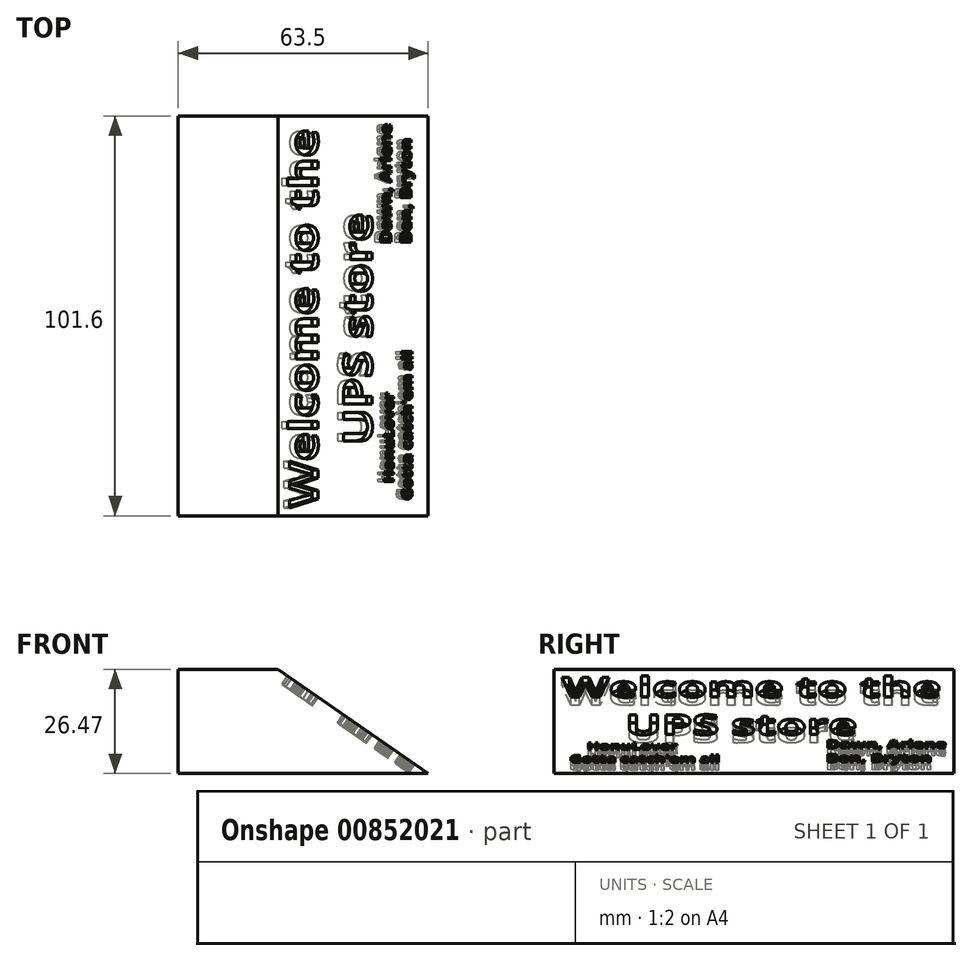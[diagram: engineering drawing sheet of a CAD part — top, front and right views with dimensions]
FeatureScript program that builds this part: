
annotation { "Feature Type Name" : "Feature", "Feature Type Description" : "" }
export const myFeature = defineFeature(function(context is Context, id is Id, definition is map)
    precondition{}
    {
        {
            var Q0;
            Q0=qCreatedBy(makeId("Front.planeOp"),FACE);
            var sketch = newSketch(context, id + "F0", { "sketchPlane" : qUnion([Q0])});
            skLineSegment(sketch, "E0", {"start": v(38.9, 0) * mm, "end": v(0.8, 26.47) * mm});
            skLineSegment(sketch, "E1", {"start": v(0.8, 26.47) * mm, "end": v(-24.6, 26.47) * mm});
            skLineSegment(sketch, "E2", {"start": v(-24.6, 26.47) * mm, "end": v(-24.6, 0) * mm});
            skLineSegment(sketch, "E3", {"start": v(-24.6, 0) * mm, "end": v(38.9, 0) * mm});
            skSolve(sketch);
        }
        {
            var Q0;
            Q0 = qSketchRegion(id + "F0", true);
            extrude(context, id + "F1", {"entities" : qUnion([Q0]), "depth" : 101.6 * mm, "offsetDistance" : 25.4 * mm});
        }
        {
            var Q0;
            Q0=makeQuery(id+"F1.opExtrude","SWEPT_FACE",FACE,{"disambiguationData":[OSD([sQuery(id+"F0.wireOp",EDGE,"E0")])]});
            var sketch = newSketch(context, id + "F2", { "sketchPlane" : qUnion([Q0])});
            skText(sketch, "E4", { "text": "Welcome to the\n     UPS store", "fontName": "OpenSans-Bold.ttf"});
            skText(sketch, "E5", { "text": "Dawn, Arlene\nBen, Bryton\n", "fontName": "OpenSans-Bold.ttf"});
            skText(sketch, "E6", { "text": "    HonuLover\nGotta catch\'em all", "fontName": "OpenSans-Bold.ttf"});
            const initialGuessF2  = {"E4": [-0.00214, -0.09955, 0, 1, 0.00886], "E5": [0.0205, -0.03238, 0, 1, 0.00327], "E6": [0.02123, -0.0976, 0, 1, 0.00301]};
            skSetInitialGuess(sketch, initialGuessF2);
            skSolve(sketch);
        }
        {
            var Q0;
            Q0 = qSketchRegion(id + "F2", true);
            extrude(context, id + "F3", {"entities" : qUnion([Q0]), "operationType" : NewBodyOperationType.REMOVE, "oppositeDirection" : true, "depth" : 2.54 * mm, "offsetDistance" : 25.4 * mm});
        }
    });
